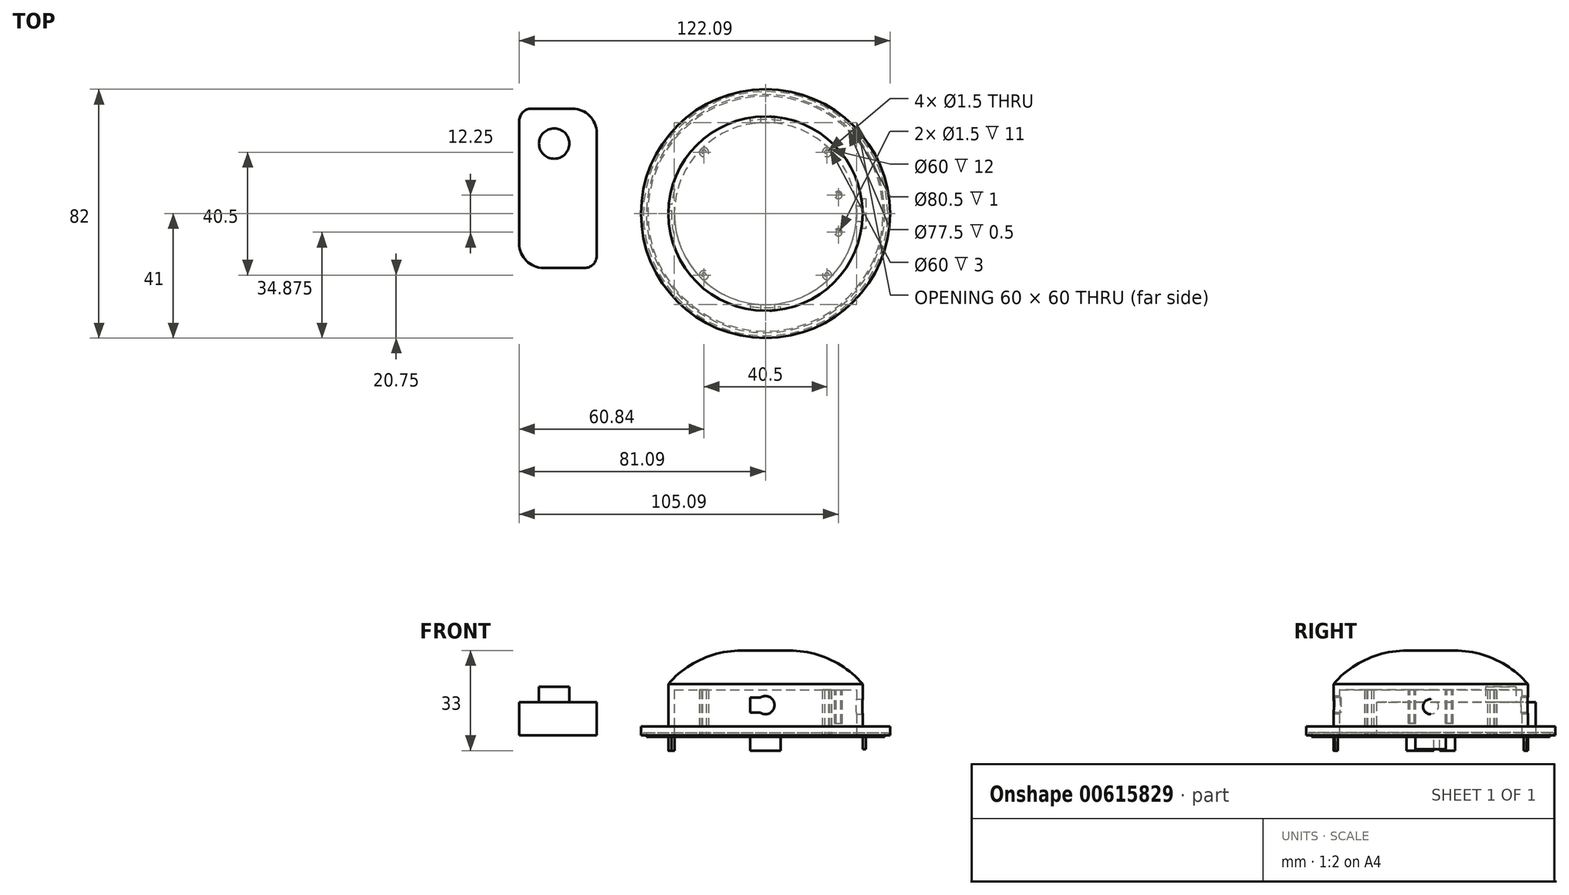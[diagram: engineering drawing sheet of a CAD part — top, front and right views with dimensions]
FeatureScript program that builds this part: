
annotation { "Feature Type Name" : "Feature", "Feature Type Description" : "" }
export const myFeature = defineFeature(function(context is Context, id is Id, definition is map)
    precondition{}
    {
        {
            var Q0;
            Q0=qCreatedBy(makeId("Top.planeOp"),FACE);
            var sketch = newSketch(context, id + "F0", { "sketchPlane" : qUnion([Q0])});
            skCircle(sketch, "E0", {"center": v(0, 0) * mm, "radius": 41 * mm});
            skSolve(sketch);
        }
        {
            var Q0;
            Q0 = qSketchRegion(id + "F0", true);
            extrude(context, id + "F1", {"entities" : qUnion([Q0]), "depth" : 3 * mm, "offsetDistance" : 25 * mm});
        }
        {
            var Q0;
            Q0=makeQuery(id+"F1.opExtrude","CAP_FACE",FACE,{"disambiguationData":[OSD([sQuery(id+"F0.wireOp",EDGE,"E0")])],"isStart":false});
            var sketch = newSketch(context, id + "F2", { "sketchPlane" : qUnion([Q0])});
            skCircle(sketch, "E1", {"center": v(0, 0) * mm, "radius": 32 * mm});
            skSolve(sketch);
        }
        {
            var Q0;
            Q0=makeQuery(id+"F2.imprint","IMPRINT",FACE,{"disambiguationData":[TD([[makeQuery(id+"F2.imprint","IMPRINT",EDGE,{"derivedFrom":sQuery(id+"F2.wireOp",EDGE,"E1")}),1.0]])]});
            extrude(context, id + "F3", {"entities" : qUnion([Q0]), "depth" : 14 * mm, "offsetDistance" : 25 * mm});
        }
        {
            var Q0;
            Q0=makeQuery(id+"F3.opExtrude","CAP_FACE",FACE,{"disambiguationData":[OSD([sQuery(id+"F2.wireOp",EDGE,"E1")])],"isStart":false});
            var sketch = newSketch(context, id + "F4", { "sketchPlane" : qUnion([Q0])});
            skCircle(sketch, "E2", {"center": v(0, 0) * mm, "radius": 32 * mm});
            skSolve(sketch);
        }
        {
            var Q0;
            Q0 = qSketchRegion(id + "F4", true);
            extrude(context, id + "F5", {"entities" : qUnion([Q0]), "depth" : 11 * mm, "offsetDistance" : 25 * mm});
        }
        {
            var Q0;
            Q0=makeQuery(id+"F5.opExtrude","CAP_EDGE",EDGE,{"disambiguationData":[OSD([sQuery(id+"F4.wireOp",EDGE,"E2")])],"isStart":false});
            fillet(context, id + "F6", {"entities" : qUnion([Q0]), "radius" : 32 * mm, "tangentPropagation" : true, "allowEdgeOverflow" : false});
        }
        {
            var Q0;
            Q0=qCreatedBy(makeId("Front.planeOp"),FACE);
            cPlane(context, id + "F7", {"entities" : qUnion([Q0]), "cplaneType" : CPlaneType.OFFSET, "offset" : 55.4 * mm, "width" : 150 * mm, "height" : 150 * mm});
        }
        {
            var Q0;
            Q0=qCreatedBy(id+"F7.planeOp",FACE);
            var sketch = newSketch(context, id + "F8", { "sketchPlane" : qUnion([Q0])});
            skCircle(sketch, "E3", {"center": v(-0.01, 10) * mm, "radius": 3 * mm});
            skLineSegment(sketch, "E4", {"start": v(-5.01, 10) * mm, "end": v(-5.01, 12.5) * mm});
            skLineSegment(sketch, "E5", {"start": v(-5.01, 12.5) * mm, "end": v(-1.67, 12.5) * mm});
            skLineSegment(sketch, "E6", {"start": v(-1.67, 7.5) * mm, "end": v(-5.01, 7.5) * mm});
            skLineSegment(sketch, "E7", {"start": v(-5.01, 7.5) * mm, "end": v(-5.01, 10) * mm});
            skSolve(sketch);
        }
        {
            var Q0;
            {var subQ0=sQuery(id+"F8.wireOp",EDGE,"E3");var subQ1=makeQuery(id+"F8.imprint","INTERSECT",VERTEX,{"derivedFrom":[subQ0,sQuery(id+"F8.wireOp",EDGE,"E5")]});Q0=makeQuery(id+"F8.imprint","IMPRINT",FACE,{"disambiguationData":[TD([[makeQuery(id+"F8.imprint","IMPRINT",EDGE,{"disambiguationData":[TD([[subQ1,-1.0]])],"derivedFrom":subQ0}),1.0]])]});}
            var Q1;
            Q1=makeQuery(id+"F8.imprint","IMPRINT",FACE,{"disambiguationData":[TD([[makeQuery(id+"F8.imprint","IMPRINT",EDGE,{"derivedFrom":sQuery(id+"F8.wireOp",EDGE,"E4")}),-1.0]])]});
            extrude(context, id + "F9", {"entities" : qUnion([Q0, Q1]), "operationType" : NewBodyOperationType.REMOVE, "oppositeDirection" : true, "depth" : 120.3 * mm, "offsetDistance" : 25 * mm});
        }
        {
            var Q0;
            Q0=qCreatedBy(makeId("Right.planeOp"),FACE);
            cPlane(context, id + "F10", {"entities" : qUnion([Q0]), "cplaneType" : CPlaneType.OFFSET, "offset" : 56.8 * mm, "width" : 150 * mm, "height" : 150 * mm});
        }
        {
            var Q0;
            Q0=qCreatedBy(id+"F10.planeOp",FACE);
            var sketch = newSketch(context, id + "F11", { "sketchPlane" : qUnion([Q0])});
            skCircle(sketch, "E8", {"center": v(0, 9.5) * mm, "radius": 2.5 * mm});
            skSolve(sketch);
        }
        {
            var Q0;
            Q0=makeQuery(id+"F11.imprint","IMPRINT",FACE,{"disambiguationData":[TD([[makeQuery(id+"F11.imprint","IMPRINT",EDGE,{"derivedFrom":sQuery(id+"F11.wireOp",EDGE,"E8")}),1.0]])]});
            extrude(context, id + "F12", {"entities" : qUnion([Q0]), "operationType" : NewBodyOperationType.REMOVE, "oppositeDirection" : true, "depth" : 58.4 * mm, "offsetDistance" : 25 * mm});
        }
        {
            var Q0;
            Q0=makeQuery(id+"F1.opExtrude","CAP_FACE",FACE,{"disambiguationData":[OSD([sQuery(id+"F0.wireOp",EDGE,"E0")])],"isStart":true});
            var sketch = newSketch(context, id + "F13", { "sketchPlane" : qUnion([Q0])});
            skCircle(sketch, "E9", {"center": v(0, 0) * mm, "radius": 40.25 * mm});
            skCircle(sketch, "E10", {"center": v(0, 0) * mm, "radius": 39.25 * mm});
            skSolve(sketch);
        }
        {
            var Q0;
            Q0=makeQuery(id+"F13.imprint","IMPRINT",FACE,{"disambiguationData":[TD([[makeQuery(id+"F13.imprint","IMPRINT",EDGE,{"derivedFrom":sQuery(id+"F13.wireOp",EDGE,"E9")}),1.0]])]});
            extrude(context, id + "F14", {"entities" : qUnion([Q0]), "operationType" : NewBodyOperationType.REMOVE, "oppositeDirection" : true, "depth" : 1 * mm, "offsetDistance" : 25 * mm});
        }
        {
            var Q0;
            Q0=makeQuery(id+"F14.boolean.opBoolean","SPLIT",FACE,{"disambiguationData":[TD([makeQuery(id+"F14.opExtrude","SWEPT_FACE",FACE,{"disambiguationData":[OSD([sQuery(id+"F13.wireOp",EDGE,"E10")])]})])],"derivedFrom":makeQuery(id+"F1.opExtrude","CAP_FACE",FACE,{"disambiguationData":[OSD([sQuery(id+"F0.wireOp",EDGE,"E0")])],"isStart":true})});
            var sketch = newSketch(context, id + "F15", { "sketchPlane" : qUnion([Q0])});
            skCircle(sketch, "E11", {"center": v(0, 0) * mm, "radius": 38.75 * mm});
            skSolve(sketch);
        }
        {
            var Q0;
            Q0=makeQuery(id+"F15.imprint","IMPRINT",FACE,{"disambiguationData":[TD([[makeQuery(id+"F15.imprint","IMPRINT",EDGE,{"derivedFrom":sQuery(id+"F15.wireOp",EDGE,"E11")}),-1.0]])]});
            extrude(context, id + "F16", {"entities" : qUnion([Q0]), "operationType" : NewBodyOperationType.ADD, "depth" : .5 * mm, "offsetDistance" : 25 * mm});
        }
        {
            var Q0;
            Q0=makeQuery(id+"F14.boolean.opBoolean","SPLIT",FACE,{"disambiguationData":[TD([makeQuery(id+"F14.opExtrude","SWEPT_FACE",FACE,{"disambiguationData":[OSD([sQuery(id+"F13.wireOp",EDGE,"E10")])]})])],"derivedFrom":makeQuery(id+"F1.opExtrude","CAP_FACE",FACE,{"disambiguationData":[OSD([sQuery(id+"F0.wireOp",EDGE,"E0")])],"isStart":true})});
            var sketch = newSketch(context, id + "F17", { "sketchPlane" : qUnion([Q0])});
            skCircle(sketch, "E12", {"center": v(0, 0) * mm, "radius": 30 * mm});
            skSolve(sketch);
        }
        {
            var Q0;
            Q0=makeQuery(id+"F17.imprint","IMPRINT",FACE,{"disambiguationData":[TD([[makeQuery(id+"F17.imprint","IMPRINT",EDGE,{"derivedFrom":sQuery(id+"F17.wireOp",EDGE,"E12")}),1.0]])]});
            extrude(context, id + "F18", {"entities" : qUnion([Q0]), "operationType" : NewBodyOperationType.REMOVE, "oppositeDirection" : true, "depth" : 15 * mm, "offsetDistance" : 25 * mm});
        }
        {
            var Q0;
            Q0=makeQuery(id+"F14.boolean.opBoolean","SPLIT",FACE,{"disambiguationData":[TD([makeQuery(id+"F14.opExtrude","SWEPT_FACE",FACE,{"disambiguationData":[OSD([sQuery(id+"F13.wireOp",EDGE,"E10")])]})])],"derivedFrom":makeQuery(id+"F1.opExtrude","CAP_FACE",FACE,{"disambiguationData":[OSD([sQuery(id+"F0.wireOp",EDGE,"E0")])],"isStart":true})});
            var sketch = newSketch(context, id + "F19", { "sketchPlane" : qUnion([Q0])});
            skCircle(sketch, "E13", {"center": v(0, 0) * mm, "radius": 41 * mm});
            skLineSegment(sketch, "E14", {"start": v(32, 0) * mm, "end": v(32, -5) * mm});
            skLineSegment(sketch, "E15", {"start": v(32, -5) * mm, "end": v(33, -5) * mm});
            skLineSegment(sketch, "E16", {"start": v(33, -5) * mm, "end": v(33, 5) * mm});
            skLineSegment(sketch, "E17", {"start": v(33, 5) * mm, "end": v(32, 5) * mm});
            skLineSegment(sketch, "E18", {"start": v(32, 5) * mm, "end": v(32, 0) * mm});
            skSolve(sketch);
        }
        {
            var Q0;
            Q0=makeQuery(id+"F19.imprint","IMPRINT",FACE,{"disambiguationData":[TD([[makeQuery(id+"F19.imprint","IMPRINT",EDGE,{"derivedFrom":sQuery(id+"F19.wireOp",EDGE,"E14")}),1.0]])]});
            extrude(context, id + "F20", {"entities" : qUnion([Q0]), "operationType" : NewBodyOperationType.ADD, "depth" : 4.5 * mm, "offsetDistance" : 25 * mm});
        }
        {
            var Q0;
            Q0=makeQuery(id+"F18.boolean.opBoolean","COPY",FACE,{"derivedFrom":makeQuery(id+"F18.opExtrude","CAP_FACE",FACE,{"disambiguationData":[OSD([sQuery(id+"F17.wireOp",EDGE,"E12")])],"isStart":false})});
            var sketch = newSketch(context, id + "F21", { "sketchPlane" : qUnion([Q0])});
            skCircle(sketch, "E19", {"center": v(0, 0) * mm, "radius": 30 * mm});
            skLineSegment(sketch, "E20", {"start": v(30, 0) * mm, "end": v(24, 0) * mm});
            skLineSegment(sketch, "E21", {"start": v(24, 0) * mm, "end": v(24, 6.12) * mm});
            skLineSegment(sketch, "E22", {"start": v(24, 0) * mm, "end": v(24, -6.13) * mm});
            skCircle(sketch, "E23", {"center": v(24, 6.12) * mm, "radius": 0.75 * mm});
            skCircle(sketch, "E24", {"center": v(24, 6.12) * mm, "radius": 1.25 * mm});
            skCircle(sketch, "E25", {"center": v(24, -6.13) * mm, "radius": 0.75 * mm});
            skCircle(sketch, "E26", {"center": v(24, -6.13) * mm, "radius": 1.25 * mm});
            skSolve(sketch);
        }
        {
            var Q0;
            Q0=makeQuery(id+"F21.imprint","IMPRINT",FACE,{"disambiguationData":[TD([[makeQuery(id+"F21.imprint","IMPRINT",EDGE,{"derivedFrom":sQuery(id+"F21.wireOp",EDGE,"E23")}),-1.0]])]});
            var Q1;
            Q1=makeQuery(id+"F21.imprint","IMPRINT",FACE,{"disambiguationData":[TD([[makeQuery(id+"F21.imprint","IMPRINT",EDGE,{"derivedFrom":sQuery(id+"F21.wireOp",EDGE,"E25")}),-1.0]])]});
            var Q2;
            Q2=makeQuery(id+"F14.boolean.opBoolean","SPLIT",FACE,{"disambiguationData":[TD([makeQuery(id+"F14.opExtrude","SWEPT_FACE",FACE,{"disambiguationData":[OSD([sQuery(id+"F13.wireOp",EDGE,"E10")])]})])],"derivedFrom":makeQuery(id+"F1.opExtrude","CAP_FACE",FACE,{"disambiguationData":[OSD([sQuery(id+"F0.wireOp",EDGE,"E0")])],"isStart":true})});
            extrude(context, id + "F22", {"entities" : qUnion([Q0, Q1]), "operationType" : NewBodyOperationType.ADD, "depth" : 11 * mm, "endBoundEntityFace" : qUnion([Q2]), "offsetDistance" : 25 * mm});
        }
        {
            var Q0;
            Q0=makeQuery(id+"F14.boolean.opBoolean","SPLIT",FACE,{"disambiguationData":[TD([makeQuery(id+"F14.opExtrude","SWEPT_FACE",FACE,{"disambiguationData":[OSD([sQuery(id+"F13.wireOp",EDGE,"E10")])]})])],"derivedFrom":makeQuery(id+"F1.opExtrude","CAP_FACE",FACE,{"disambiguationData":[OSD([sQuery(id+"F0.wireOp",EDGE,"E0")])],"isStart":true})});
            var sketch = newSketch(context, id + "F23", { "sketchPlane" : qUnion([Q0])});
            skLineSegment(sketch, "E27", {"start": v(0, 0) * mm, "end": v(-20.25, 0) * mm});
            skLineSegment(sketch, "E28", {"start": v(-20.25, 0) * mm, "end": v(-20.25, 20.25) * mm});
            skLineSegment(sketch, "E29", {"start": v(-20.25, 20.25) * mm, "end": v(0, 20.25) * mm});
            skLineSegment(sketch, "E30", {"start": v(0, 20.25) * mm, "end": v(20.25, 20.25) * mm});
            skLineSegment(sketch, "E31", {"start": v(20.25, 20.25) * mm, "end": v(20.25, 0) * mm});
            skLineSegment(sketch, "E32", {"start": v(20.25, 0) * mm, "end": v(20.25, -20.25) * mm});
            skLineSegment(sketch, "E33", {"start": v(20.25, -20.25) * mm, "end": v(0, -20.25) * mm});
            skLineSegment(sketch, "E34", {"start": v(0, -20.25) * mm, "end": v(-20.25, -20.25) * mm});
            skLineSegment(sketch, "E35", {"start": v(-20.25, -20.25) * mm, "end": v(-20.25, 0) * mm});
            skCircle(sketch, "E36", {"center": v(-20.25, 20.25) * mm, "radius": 0.75 * mm});
            skCircle(sketch, "E37", {"center": v(-20.25, 20.25) * mm, "radius": 1.5 * mm});
            skCircle(sketch, "E38", {"center": v(20.25, 20.25) * mm, "radius": 0.75 * mm});
            skCircle(sketch, "E39", {"center": v(20.25, 20.25) * mm, "radius": 1.5 * mm});
            skCircle(sketch, "E40", {"center": v(20.25, -20.25) * mm, "radius": 0.75 * mm});
            skCircle(sketch, "E41", {"center": v(20.25, -20.25) * mm, "radius": 1.5 * mm});
            skCircle(sketch, "E42", {"center": v(-20.25, -20.25) * mm, "radius": 0.75 * mm});
            skCircle(sketch, "E43", {"center": v(-20.25, -20.25) * mm, "radius": 1.5 * mm});
            skSolve(sketch);
        }
        {
            var Q0;
            {var subQ0=sQuery(id+"F23.wireOp",EDGE,"E39");var subQ1=sQuery(id+"F23.wireOp",EDGE,"E30");var subQ2=makeQuery(id+"F23.imprint","INTERSECT",VERTEX,{"derivedFrom":[subQ1,subQ0]});Q0=makeQuery(id+"F23.imprint","IMPRINT",FACE,{"disambiguationData":[TD([[makeQuery(id+"F23.imprint","IMPRINT",EDGE,{"disambiguationData":[TD([[subQ2,-1.0]])],"derivedFrom":subQ1}),-1.0]])]});}
            var Q1;
            {var subQ0=sQuery(id+"F23.wireOp",EDGE,"E39");var subQ1=sQuery(id+"F23.wireOp",EDGE,"E30");var subQ2=makeQuery(id+"F23.imprint","INTERSECT",VERTEX,{"derivedFrom":[subQ1,subQ0]});Q1=makeQuery(id+"F23.imprint","IMPRINT",FACE,{"disambiguationData":[TD([[makeQuery(id+"F23.imprint","IMPRINT",EDGE,{"disambiguationData":[TD([[subQ2,-1.0]])],"derivedFrom":subQ1}),1.0]])]});}
            var Q2;
            {var subQ0=sQuery(id+"F23.wireOp",EDGE,"E41");var subQ6=sQuery(id+"F23.wireOp",EDGE,"E32");var subQ10=makeQuery(id+"F23.imprint","INTERSECT",VERTEX,{"derivedFrom":[subQ6,subQ0]});Q2=makeQuery(id+"F23.imprint","IMPRINT",FACE,{"disambiguationData":[TD([[makeQuery(id+"F23.imprint","IMPRINT",EDGE,{"disambiguationData":[TD([[subQ10,-1.0]])],"derivedFrom":subQ6}),1.0]])]});}
            var Q3;
            {var subQ0=sQuery(id+"F23.wireOp",EDGE,"E41");var subQ1=sQuery(id+"F23.wireOp",EDGE,"E32");var subQ2=makeQuery(id+"F23.imprint","INTERSECT",VERTEX,{"derivedFrom":[subQ1,subQ0]});Q3=makeQuery(id+"F23.imprint","IMPRINT",FACE,{"disambiguationData":[TD([[makeQuery(id+"F23.imprint","IMPRINT",EDGE,{"disambiguationData":[TD([[subQ2,-1.0]])],"derivedFrom":subQ1}),-1.0]])]});}
            var Q4;
            {var subQ0=sQuery(id+"F23.wireOp",EDGE,"E43");var subQ1=sQuery(id+"F23.wireOp",EDGE,"E34");var subQ2=makeQuery(id+"F23.imprint","INTERSECT",VERTEX,{"derivedFrom":[subQ1,subQ0]});Q4=makeQuery(id+"F23.imprint","IMPRINT",FACE,{"disambiguationData":[TD([[makeQuery(id+"F23.imprint","IMPRINT",EDGE,{"disambiguationData":[TD([[subQ2,-1.0]])],"derivedFrom":subQ1}),-1.0]])]});}
            var Q5;
            {var subQ0=sQuery(id+"F23.wireOp",EDGE,"E43");var subQ6=sQuery(id+"F23.wireOp",EDGE,"E34");var subQ9=makeQuery(id+"F23.imprint","INTERSECT",VERTEX,{"derivedFrom":[subQ6,subQ0]});Q5=makeQuery(id+"F23.imprint","IMPRINT",FACE,{"disambiguationData":[TD([[makeQuery(id+"F23.imprint","IMPRINT",EDGE,{"disambiguationData":[TD([[subQ9,-1.0]])],"derivedFrom":subQ6}),1.0]])]});}
            var Q6;
            {var subQ0=sQuery(id+"F23.wireOp",EDGE,"E37");var subQ1=sQuery(id+"F23.wireOp",EDGE,"E28");var subQ2=makeQuery(id+"F23.imprint","INTERSECT",VERTEX,{"derivedFrom":[subQ1,subQ0]});Q6=makeQuery(id+"F23.imprint","IMPRINT",FACE,{"disambiguationData":[TD([[makeQuery(id+"F23.imprint","IMPRINT",EDGE,{"disambiguationData":[TD([[subQ2,-1.0]])],"derivedFrom":subQ1}),-1.0]])]});}
            var Q7;
            {var subQ1=sQuery(id+"F23.wireOp",EDGE,"E28");var subQ5=sQuery(id+"F23.wireOp",EDGE,"E37");var subQ9=makeQuery(id+"F23.imprint","INTERSECT",VERTEX,{"derivedFrom":[subQ1,subQ5]});Q7=makeQuery(id+"F23.imprint","IMPRINT",FACE,{"disambiguationData":[TD([[makeQuery(id+"F23.imprint","IMPRINT",EDGE,{"disambiguationData":[TD([[subQ9,-1.0]])],"derivedFrom":subQ1}),1.0]])]});}
            var Q8;
            {var subQ3=sQuery(id+"F17.wireOp",EDGE,"E12");var subQ4=makeQuery(id+"F18.opExtrude","CAP_FACE",FACE,{"disambiguationData":[OSD([subQ3])],"isStart":false});Q8=makeQuery(id+"F22.boolean.opBoolean","SPLIT",FACE,{"disambiguationData":[TD([makeQuery(id+"F22.opExtrude","SWEPT_FACE",FACE,{"disambiguationData":[OSD([sQuery(id+"F21.wireOp",EDGE,"E24")])]})])],"derivedFrom":makeQuery(id+"F18.boolean.opBoolean","COPY",FACE,{"derivedFrom":subQ4})});}
            extrude(context, id + "F24", {"entities" : qUnion([Q0, Q1, Q2, Q3, Q4, Q5, Q6, Q7]), "endBound" : BoundingType.UP_TO_SURFACE, "oppositeDirection" : true, "depth" : 25 * mm, "endBoundEntityFace" : qUnion([Q8]), "offsetDistance" : 25 * mm});
        }
        {
            var Q0;
            Q0=makeQuery(id+"F14.boolean.opBoolean","SPLIT",FACE,{"disambiguationData":[TD([makeQuery(id+"F14.opExtrude","SWEPT_FACE",FACE,{"disambiguationData":[OSD([sQuery(id+"F13.wireOp",EDGE,"E10")])]})])],"derivedFrom":makeQuery(id+"F1.opExtrude","CAP_FACE",FACE,{"disambiguationData":[OSD([sQuery(id+"F0.wireOp",EDGE,"E0")])],"isStart":true})});
            var sketch = newSketch(context, id + "F25", { "sketchPlane" : qUnion([Q0])});
            skCircle(sketch, "E44", {"center": v(0, 0) * mm, "radius": 32 * mm});
            skCircle(sketch, "E45", {"center": v(0, 0) * mm, "radius": 31 * mm});
            skLineSegment(sketch, "E46", {"start": v(5, 32) * mm, "end": v(5, 28.1) * mm});
            skLineSegment(sketch, "E47", {"start": v(-5, 28.1) * mm, "end": v(-5, 32) * mm});
            skLineSegment(sketch, "E48", {"start": v(-5, 28.1) * mm, "end": v(-5, -58.1) * mm});
            skLineSegment(sketch, "E49", {"start": v(5, -58.1) * mm, "end": v(5, 28.1) * mm});
            skLineSegment(sketch, "E50", {"start": v(-31, 0) * mm, "end": v(-32, 0) * mm});
            skLineSegment(sketch, "E51", {"start": v(-32, 0) * mm, "end": v(-32, 8) * mm});
            skLineSegment(sketch, "E52", {"start": v(-32, 8) * mm, "end": v(-27.16, 8) * mm});
            skLineSegment(sketch, "E53", {"start": v(-27.16, 8) * mm, "end": v(-27.16, -8) * mm});
            skLineSegment(sketch, "E54", {"start": v(-27.16, -8) * mm, "end": v(-32, -8) * mm});
            skLineSegment(sketch, "E55", {"start": v(-32, -8) * mm, "end": v(-32, 0) * mm});
            skLineSegment(sketch, "E56", {"start": v(-32, 8) * mm, "end": v(-32, -1) * mm});
            skLineSegment(sketch, "E57", {"start": v(-32, -1) * mm, "end": v(-30.98, -1) * mm});
            skLineSegment(sketch, "E58", {"start": v(-30.98, -1) * mm, "end": v(-28.86, -1) * mm});
            skLineSegment(sketch, "E59", {"start": v(-28.86, -1) * mm, "end": v(-28.86, -3) * mm});
            skLineSegment(sketch, "E60", {"start": v(-28.86, -3) * mm, "end": v(-33.32, -3) * mm});
            skSolve(sketch);
        }
        {
            var Q0;
            {var subQ0=sQuery(id+"F25.wireOp",EDGE,"E47");var subQ1=sQuery(id+"F25.wireOp",EDGE,"E44");var subQ2=makeQuery(id+"F25.imprint","INTERSECT",VERTEX,{"derivedFrom":[subQ1,subQ0]});Q0=makeQuery(id+"F25.imprint","IMPRINT",FACE,{"disambiguationData":[TD([[makeQuery(id+"F25.imprint","IMPRINT",EDGE,{"disambiguationData":[TD([[subQ2,1.0]])],"derivedFrom":subQ1}),1.0]])]});}
            var Q1;
            {var subQ0=sQuery(id+"F25.wireOp",EDGE,"E48");var subQ1=sQuery(id+"F25.wireOp",EDGE,"E44");var subQ2=makeQuery(id+"F25.imprint","INTERSECT",VERTEX,{"derivedFrom":[subQ1,subQ0]});Q1=makeQuery(id+"F25.imprint","IMPRINT",FACE,{"disambiguationData":[TD([[makeQuery(id+"F25.imprint","IMPRINT",EDGE,{"disambiguationData":[TD([[subQ2,-1.0]])],"derivedFrom":subQ1}),1.0]])]});}
            var Q2;
            {var subQ0=sQuery(id+"F25.wireOp",EDGE,"E60");var subQ1=sQuery(id+"F25.wireOp",EDGE,"E44");var subQ2=makeQuery(id+"F25.imprint","INTERSECT",VERTEX,{"derivedFrom":[subQ1,subQ0]});Q2=makeQuery(id+"F25.imprint","IMPRINT",FACE,{"disambiguationData":[TD([[makeQuery(id+"F25.imprint","IMPRINT",EDGE,{"disambiguationData":[TD([[subQ2,-1.0]])],"derivedFrom":subQ1}),1.0]])]});}
            var Q3;
            {var subQ0=sQuery(id+"F25.wireOp",EDGE,"E50");Q3=makeQuery(id+"F25.imprint","IMPRINT",FACE,{"disambiguationData":[TD([[makeQuery(id+"F25.imprint","IMPRINT",EDGE,{"derivedFrom":subQ0}),-1.0]])]});}
            var Q4;
            {var subQ0=sQuery(id+"F25.wireOp",EDGE,"E50");Q4=makeQuery(id+"F25.imprint","IMPRINT",FACE,{"disambiguationData":[TD([[makeQuery(id+"F25.imprint","IMPRINT",EDGE,{"derivedFrom":subQ0}),1.0]])]});}
            extrude(context, id + "F26", {"entities" : qUnion([Q0, Q1, Q2, Q3, Q4]), "operationType" : NewBodyOperationType.ADD, "depth" : 5 * mm, "offsetDistance" : 25 * mm});
        }
        {
            var Q0;
            Q0=qCreatedBy(makeId("Top.planeOp"),FACE);
            var sketch = newSketch(context, id + "F27", { "sketchPlane" : qUnion([Q0])});
            skLineSegment(sketch, "E61", {"start": v(-63.6, 34.6) * mm, "end": v(-77.1, 34.6) * mm});
            skLineSegment(sketch, "E62", {"start": v(-81.1, 30.6) * mm, "end": v(-81.1, -9.9) * mm});
            skLineSegment(sketch, "E63", {"start": v(-73.1, -17.9) * mm, "end": v(-59.6, -17.9) * mm});
            skLineSegment(sketch, "E64", {"start": v(-55.6, -13.9) * mm, "end": v(-55.6, 26.6) * mm});
            skPoint(sketch, "E65.visualSharp", {"position": v(-55.6, 34.6) * mm});
            skArc(sketch, "E65.filletArc", {"start": v(-55.6, 26.6) * mm, "mid": v(-57.94, 32.25) * mm, "end": v(-63.6, 34.6) * mm});
            skPoint(sketch, "E66.visualSharp", {"position": v(-81.1, 34.6) * mm});
            skArc(sketch, "E66.filletArc", {"start": v(-77.1, 34.6) * mm, "mid": v(-79.92, 33.42) * mm, "end": v(-81.1, 30.6) * mm});
            skPoint(sketch, "E67.visualSharp", {"position": v(-55.6, -17.9) * mm});
            skArc(sketch, "E67.filletArc", {"start": v(-59.6, -17.9) * mm, "mid": v(-56.76, -16.73) * mm, "end": v(-55.6, -13.9) * mm});
            skPoint(sketch, "E68.visualSharp", {"position": v(-81.1, -17.9) * mm});
            skArc(sketch, "E68.filletArc", {"start": v(-81.1, -9.9) * mm, "mid": v(-78.75, -15.56) * mm, "end": v(-73.1, -17.9) * mm});
            skSolve(sketch);
        }
        {
            var Q0;
            Q0=makeQuery(id+"F27.imprint","IMPRINT",FACE,{"disambiguationData":[TD([[makeQuery(id+"F27.imprint","IMPRINT",EDGE,{"derivedFrom":sQuery(id+"F27.wireOp",EDGE,"E61")}),1.0]])]});
            extrude(context, id + "F28", {"entities" : qUnion([Q0]), "depth" : 11 * mm, "offsetDistance" : 25 * mm});
        }
        {
            var Q0;
            Q0=makeQuery(id+"F28.opExtrude","CAP_FACE",FACE,{"disambiguationData":[OSD([sQuery(id+"F27.wireOp",EDGE,"E61"),sQuery(id+"F27.wireOp",EDGE,"E62"),sQuery(id+"F27.wireOp",EDGE,"E63"),sQuery(id+"F27.wireOp",EDGE,"E64"),sQuery(id+"F27.wireOp",EDGE,"E65.filletArc"),sQuery(id+"F27.wireOp",EDGE,"E66.filletArc"),sQuery(id+"F27.wireOp",EDGE,"E67.filletArc"),sQuery(id+"F27.wireOp",EDGE,"E68.filletArc")])],"isStart":false});
            var sketch = newSketch(context, id + "F29", { "sketchPlane" : qUnion([Q0])});
            skPoint(sketch, "E69.endSnap0", {"position": v(-70.34, 34.6) * mm});
            skCircle(sketch, "E70", {"center": v(-69.6, 23.1) * mm, "radius": 5 * mm});
            skSolve(sketch);
        }
        {
            var Q0;
            Q0=makeQuery(id+"F29.imprint","IMPRINT",FACE,{"disambiguationData":[TD([[makeQuery(id+"F29.imprint","IMPRINT",EDGE,{"derivedFrom":sQuery(id+"F29.wireOp",EDGE,"E70")}),1.0]])]});
            extrude(context, id + "F30", {"entities" : qUnion([Q0]), "operationType" : NewBodyOperationType.ADD, "depth" : 5 * mm, "offsetDistance" : 25 * mm});
        }
    });
